# Revit family: NBS_DudleyIndustriesLimited_SntryTwlDpnsrs_PlatinumSanitaryBagHolder
name_source: partatom
category: Furniture
revit_build: Autodesk Revit 2018 (Build: 20190510_1515(x64)
units: mm (PartAtom-declared; Revit-internal decimal feet)

## family parameters
Cut with Voids When Loaded = No
Host = Face
Room Calculation Point = No
Shared = No

## types (1)
- PlatinumSanitaryBagHolder
    AssetType = Fixed
    BIMObjectName = NBS_DudleyIndustriesLimited_SanitaryTowelDispensers_PlatinumSanitaryBagHolder
    Category = Pr_40_70_22_75:Sanitary towel dispensers
    Default Elevation = 750 mm  [stored 2.46063 ft]
    Description = Platinum sanitary bag holder
    DurationUnit = year
    Features = Innovative coating helps prevent fingerprint marks, the holder presents bags in a handy and neat, manner, supports your washroom aesthetics, sanitary disposal bags help contain waste, and keep sanitary bins clean in between services
    Finish = Brushed with clear lacquer
    HolderMaterial = NBS_DudleyIndustriesLimited_StainlessSteel_Brushed
    IfcExportAs = IfcFurnitureType
    IfcExportType = UNDEFINED
    IsBuiltIn = Yes
    ManufacturerName = Dudley Industries Limited
    ManufacturerURL = www.dudleyindustries.com
    Material = Stainless steel
    MaterialsBody = Stainless steel
    MaterialsFinishAndColour = Brushed with clear lacquer
    ModelNumber = 77021CB
    ModelReference = PlatinumSanitaryBagHolder
    NBSCertification = www.nationalbimlibrary.com/cert/r5q2yrvv
    NBSDescription = Sanitary towel dispensers
    NBSReference = 45-35-72/348
    Name = SanitaryTowelDispensers_PlatinumSanitaryBagHolder_DudleyIndustriesLimited
    NominalDepth = 48 mm  [stored 0.15748 ft]
    NominalHeight = 155 mm  [stored 0.50853 ft]
    NominalLength = 0 mm  [stored 0 ft]
    NominalWidth = 111 mm
    ProductInformation = https://www.dudleyindustries.com
    Shape = Rectangular
    Size = 111 x 155 x 48 mm
    Status = UNSET
    Style = Holder
    Uniclass2015Code = Pr_40_70_22_75
    Uniclass2015Title = Sanitary towel dispensers
    Uniclass2015Version = Products v1.18
    Version = 1
    WarrantyDescription = 10 Years
    WarrantyDurationUnit = year
    Weight = 0.27 kg

note: [stored X ft] marks values corroborated as IEEE doubles in the binary element streams (Revit-internal decimal feet)

## geometry (parser evidence)
native form markers: Sweep x2
no freeform markers — native parametric forms only
